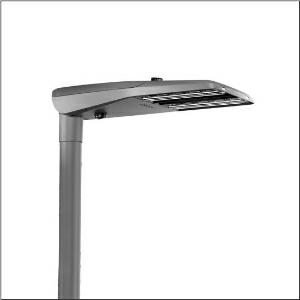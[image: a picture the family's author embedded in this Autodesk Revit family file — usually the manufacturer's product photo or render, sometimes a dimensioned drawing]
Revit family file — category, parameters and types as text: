
# Revit family: streetlight_sl_11_iq_midi___pc-r_5xc3f11y08me_2da3
name_source: partatom
category: Lighting Fixtures
units: mm (PartAtom-declared; Revit-internal decimal feet)

## family parameters
Cut with Voids When Loaded = No
Host = Face
Light Source = No
Part Type = Normal
Room Calculation Point = No
Round Connector Dimension = Use Diameter
Shared = No

## types (1)
- --- (1 x LED, 9610 lm, 123.4 W, 1800K)
    Apparent Load = 123 VA
    CIE Flux Codes = 37 73 96 100 100
    Color Rendering = 70
    Color Temperature = 1800K
    Default Elevation = 1800 mm  [stored 5.90551 ft]
    Description = Streetlight SL 11 iQ midi, mast luminaire, primary light control with 3 zone facetted reflector, of plastic, silver coated, highly specular, primary optical cover: cover, of PMMA, transparent, light distribution: PC-R, light emission: direct distribution, primary light characteristic: asymmetric, right, installation type: post-top, side-entry, lamps: LED, High Power LED, rated values: 9.610lm | 123,4W | 77,9lm/W (begin service life); end service life: 9.610lm | 130,9W; at 50% lumin. flux: 4.805lm | 54,1W | 88,8lm/W, colour temperature: 1800K, colour rendering: CRI > 70, light colour: 718, light setting 1 begin service life: 100% | 9.610lm | 123,4W | 77,9lm/W | 1.800K, light setting 1 end service life: 130,9W, further light settings possible, control: pre-setting: logarithmic dimming characteristic, Street-Remote, Auto-Match, Temp-Guard, Lumen-Switch, Night-Set, Smart-Wire, Light-Fading, Desk-Remote (wireless, voltage-free reading and setting of iQ features in the workshop via application-optimized NFC function/RFID function), optimised constant luminous flux control (CLO 2.0), with cable H07RN-F 5x 1.5mm², mains connection: 230..240V, AC, 50/60Hz, connection cable pre-assembled, cable length: 12,5m, luminaire housing, of diecast aluminium, powder-coated, Siteco® metallic grey (DB 702S), please order mast flange separately, inclination adjustable without tools: 0°, 5°, 10°, 15° (post-top) | 0°, -5°, -10°, -15° (side-entry), sealing non-destructively replaceable, multi-level sealing system, length: 780mm, width: 376mm, height: 118mm, mast flange for spigot size: 42mm (side-entry): 5XC10008XM4, 60/48mm (side-entry/post-top): 5XC10108XM2, 76/60mm (side-entry/post-top): 5XC10108XM1, equipment: Power, Smart Interface below and above, protection rating (complete): IP66, insulation class (complete): insulation class II (safety insulation), certification: CE, ENEC, ENEC+, VDE, UKCA, impact resistance: IK10, permissible operating ambient temperature for outdoor applications: -25..+50°C, standard-compliant lighting for roads and squares, Environmental Product Declaration (EPD) tested and certified by an independent institute, packaging unit: 1 piece

Light Distribution: PC-R
    Height = 118 mm
    Lamp = 1 x LED
    Lamp Light Flux = 9610 lm
    Lamp Power = 123.4 W
    Lamp count = 1
    Length = 780 mm
    Luminous efficacy = 78 lm/W
    Manufacturer = Siteco
    ModVariant = No
    Model = 5XC3F11Y08ME
    Number of Poles = 1
    OnlyDefault = Yes
    Power Factor = 1
    Product Name = Streetlight SL 11 iQ midi | PC-R
    Product group = mast luminaire | pylon top
    ProductGroupID = 6100
    Protection Class = Protection class II
    Protection Degree = IP 66
    RLX_Detail_Level = 1
    RLX_Emergency_Light_Flux = 0 lm
    RLX_Emergency_Type = 0
    RLX_Emergency_Type_DB = No
    RlxData = <blob elided: 73701 chars, md5=5f95f08c>
    Socket = socket
    Standby Power = 0 W
    System Light Flux = 9610 lm
    System Power = 123 W
    Type Comments = factory setting: luminous flux: 100 % | dim-lin: 254 | 553 mA
    Type Image = l_1004429.jpg
    URL = http://relux.com
    VarID = @adj_032340
    Voltage = 0 V
    Weight = 0.00 kg
    Width = 376 mm

note: [stored X ft] marks values corroborated as IEEE doubles in the binary element streams (Revit-internal decimal feet)

## geometry (parser evidence)
native form markers: Blend x4, Sweep x10
no freeform markers — native parametric forms only
